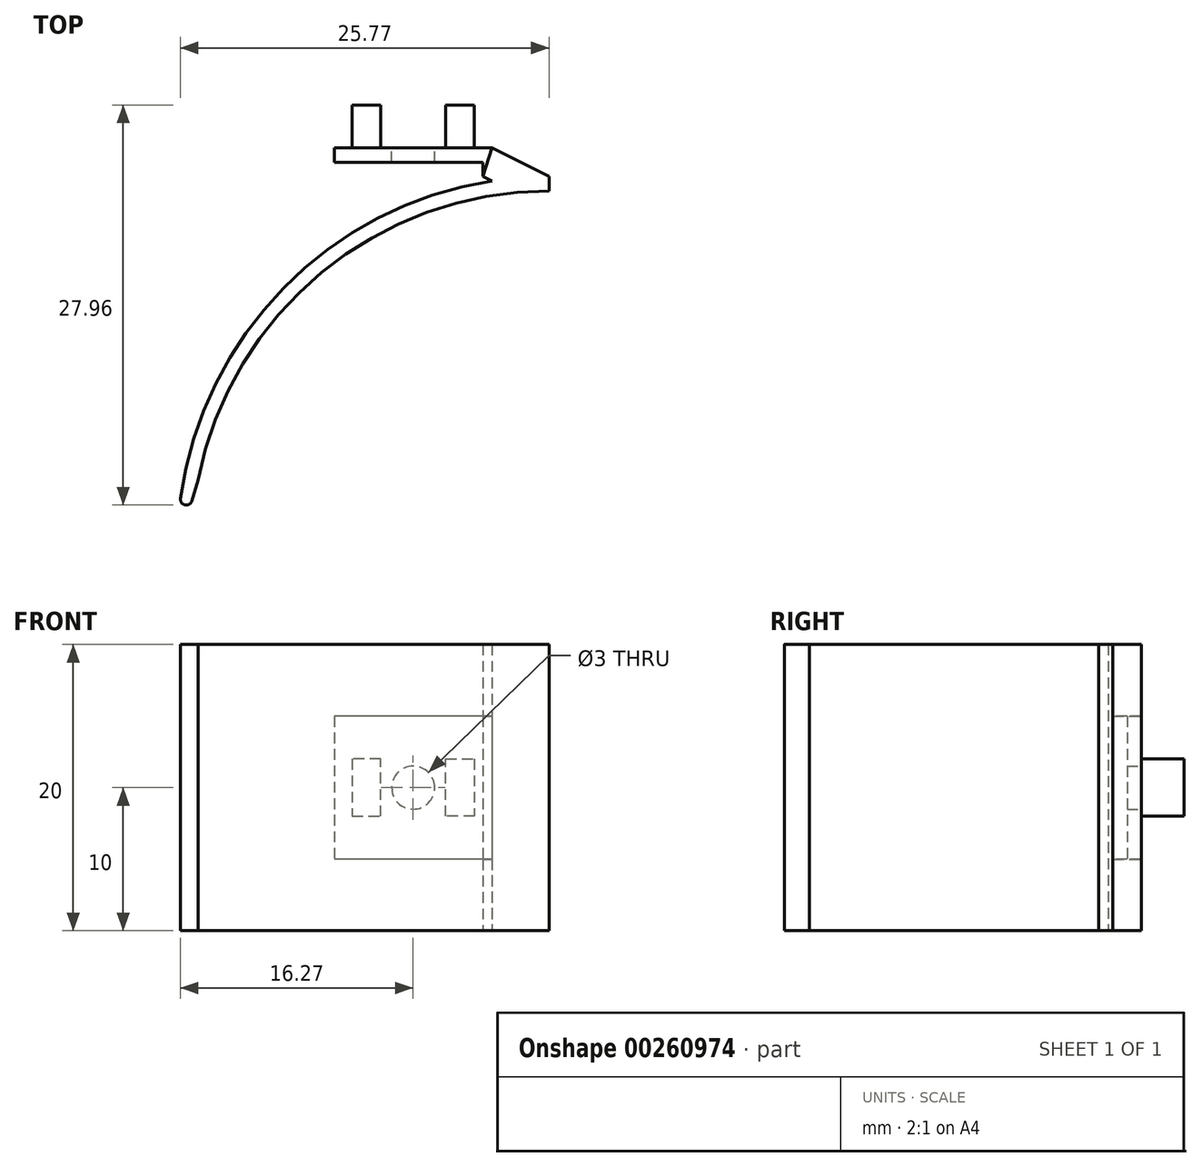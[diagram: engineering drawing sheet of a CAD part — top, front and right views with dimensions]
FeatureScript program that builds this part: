
annotation { "Feature Type Name" : "Feature", "Feature Type Description" : "" }
export const myFeature = defineFeature(function(context is Context, id is Id, definition is map)
    precondition{}
    {
        {
            var Q0;
            Q0=qCreatedBy(makeId("Top.planeOp"),FACE);
            var sketch = newSketch(context, id + "F0", { "sketchPlane" : qUnion([Q0])});
            skArc(sketch, "E0", {"start": v(0, 25) * mm, "mid": v(-15.9, 19.3) * mm, "end": v(-24.54, 4.8) * mm});
            skArc(sketch, "E1", {"start": v(-4, 25.7) * mm, "mid": v(-19.75, 16.91) * mm, "end": v(-26, 0) * mm});
            skLineSegment(sketch, "E2", {"start": v(0, 25) * mm, "end": v(0, 26) * mm});
            skLineSegment(sketch, "E3", {"start": v(-26, 0) * mm, "end": v(-24.54, 4.8) * mm});
            skLineSegment(sketch, "E4", {"start": v(-4, 28) * mm, "end": v(-15, 28) * mm});
            skLineSegment(sketch, "E5", {"start": v(-15, 28) * mm, "end": v(-15, 26) * mm});
            skLineSegment(sketch, "E6", {"start": v(-4.62, 26) * mm, "end": v(-15, 26) * mm});
            skPoint(sketch, "E7.orphan", {"position": v(-15, 25) * mm});
            skLineSegment(sketch, "E8", {"start": v(-4, 28) * mm, "end": v(0, 26) * mm});
            skLineSegment(sketch, "E9", {"start": v(-6, 28) * mm, "end": v(-8, 28) * mm});
            skLineSegment(sketch, "E10", {"start": v(-4, 25.7) * mm, "end": v(-4.62, 26) * mm});
            skSolve(sketch);
        }
        {
            var Q0;
            Q0=makeQuery(id+"F0.imprint","IMPRINT",FACE,{"disambiguationData":[TD([[makeQuery(id+"F0.imprint","IMPRINT",EDGE,{"derivedFrom":sQuery(id+"F0.wireOp",EDGE,"E0")}),-1.0]])]});
            extrude(context, id + "F1", {"entities" : qUnion([Q0]), "depth" : 20 * mm});
        }
        {
            var Q0;
            Q0=makeQuery(id+"F1.opExtrude","CAP_FACE",FACE,{"disambiguationData":[OSD([sQuery(id+"F0.wireOp",EDGE,"E0"),sQuery(id+"F0.wireOp",EDGE,"E1"),sQuery(id+"F0.wireOp",EDGE,"E2"),sQuery(id+"F0.wireOp",EDGE,"E3"),sQuery(id+"F0.wireOp",EDGE,"E4"),sQuery(id+"F0.wireOp",EDGE,"E5"),sQuery(id+"F0.wireOp",EDGE,"E6"),sQuery(id+"F0.wireOp",EDGE,"E8"),sQuery(id+"F0.wireOp",EDGE,"E9"),sQuery(id+"F0.wireOp",EDGE,"E10")])],"isStart":false});
            var sketch = newSketch(context, id + "F2", { "sketchPlane" : qUnion([Q0])});
            skLineSegment(sketch, "E11", {"start": v(-4.62, 26) * mm, "end": v(-4, 28) * mm});
            skSolve(sketch);
        }
        {
            var Q0;
            Q0=makeQuery(id+"F2.imprint","IMPRINT",FACE,{"disambiguationData":[TD([[makeQuery(id+"F2.imprint","IMPRINT",EDGE,{"derivedFrom":sQuery(id+"F2.wireOp",EDGE,"E11")}),1.0]])]});
            extrude(context, id + "F3", {"entities" : qUnion([Q0]), "operationType" : NewBodyOperationType.REMOVE, "oppositeDirection" : true, "depth" : 5 * mm});
        }
        {
            var Q0;
            Q0=makeQuery(id+"F1.opExtrude","CAP_FACE",FACE,{"disambiguationData":[OSD([sQuery(id+"F0.wireOp",EDGE,"E0"),sQuery(id+"F0.wireOp",EDGE,"E1"),sQuery(id+"F0.wireOp",EDGE,"E2"),sQuery(id+"F0.wireOp",EDGE,"E3"),sQuery(id+"F0.wireOp",EDGE,"E4"),sQuery(id+"F0.wireOp",EDGE,"E5"),sQuery(id+"F0.wireOp",EDGE,"E6"),sQuery(id+"F0.wireOp",EDGE,"E8"),sQuery(id+"F0.wireOp",EDGE,"E9"),sQuery(id+"F0.wireOp",EDGE,"E10")])],"isStart":true});
            var sketch = newSketch(context, id + "F4", { "sketchPlane" : qUnion([Q0])});
            skLineSegment(sketch, "E12", {"start": v(-4.62, -26) * mm, "end": v(-4, -28) * mm});
            skSolve(sketch);
        }
        {
            var Q0;
            Q0=makeQuery(id+"F4.imprint","IMPRINT",FACE,{"disambiguationData":[TD([[makeQuery(id+"F4.imprint","IMPRINT",EDGE,{"derivedFrom":sQuery(id+"F4.wireOp",EDGE,"E12")}),-1.0]])]});
            extrude(context, id + "F5", {"entities" : qUnion([Q0]), "operationType" : NewBodyOperationType.REMOVE, "oppositeDirection" : true, "depth" : 5 * mm});
        }
        {
            var Q0;
            Q0=makeQuery(id+"F1.opExtrude","SWEPT_FACE",FACE,{"disambiguationData":[OSD([sQuery(id+"F0.wireOp",EDGE,"E4"),sQuery(id+"F0.wireOp",EDGE,"E9")])]});
            var sketch = newSketch(context, id + "F6", { "sketchPlane" : qUnion([Q0])});
            skLineSegment(sketch, "E13", {"start": v(15, 10) * mm, "end": v(4, 10) * mm, "construction": true});
            skCircle(sketch, "E14", {"center": v(9.5, 10) * mm, "radius": 1.5 * mm});
            skSolve(sketch);
        }
        {
            var Q0;
            Q0=makeQuery(id+"F1.opExtrude","SWEPT_FACE",FACE,{"disambiguationData":[OSD([sQuery(id+"F0.wireOp",EDGE,"E4"),sQuery(id+"F0.wireOp",EDGE,"E9")])]});
            var sketch = newSketch(context, id + "F7", { "sketchPlane" : qUnion([Q0])});
            skLineSegment(sketch, "E15", {"start": v(4, 10) * mm, "end": v(15, 10) * mm, "construction": true});
            skCircle(sketch, "E16", {"center": v(9.5, 10) * mm, "radius": 1.55 * mm});
            skLineSegment(sketch, "E17", {"start": v(9.5, 10) * mm, "end": v(11.78, 10) * mm, "construction": true});
            skLineSegment(sketch, "E18", {"start": v(11.78, 10) * mm, "end": v(11.78, 12) * mm});
            skLineSegment(sketch, "E19", {"start": v(11.78, 12) * mm, "end": v(13.78, 12) * mm});
            skLineSegment(sketch, "E20", {"start": v(13.78, 12) * mm, "end": v(13.78, 8) * mm});
            skLineSegment(sketch, "E21", {"start": v(13.78, 8) * mm, "end": v(11.78, 8) * mm});
            skLineSegment(sketch, "E22", {"start": v(11.78, 8) * mm, "end": v(11.78, 10) * mm});
            skLineSegment(sketch, "E23", {"start": v(9.5, 10) * mm, "end": v(9.5, 13.7) * mm, "construction": true});
            skLineSegment(sketch, "E24.MirrorCS", {"start": v(7.22, 12) * mm, "end": v(5.22, 12) * mm});
            skLineSegment(sketch, "E25.MirrorCS", {"start": v(5.22, 12) * mm, "end": v(5.22, 8) * mm});
            skLineSegment(sketch, "E26.MirrorCS", {"start": v(5.22, 8) * mm, "end": v(7.22, 8) * mm});
            skLineSegment(sketch, "E27.MirrorCS", {"start": v(7.22, 10) * mm, "end": v(7.22, 12) * mm});
            skLineSegment(sketch, "E28.MirrorCS", {"start": v(7.22, 8) * mm, "end": v(7.22, 10) * mm});
            skSolve(sketch);
        }
        {
            var Q0;
            Q0=makeQuery(id+"F7.imprint","IMPRINT",FACE,{"disambiguationData":[TD([[makeQuery(id+"F7.imprint","IMPRINT",EDGE,{"derivedFrom":sQuery(id+"F7.wireOp",EDGE,"E18")}),-1.0]])]});
            var Q1;
            Q1=makeQuery(id+"F7.imprint","IMPRINT",FACE,{"disambiguationData":[TD([[makeQuery(id+"F7.imprint","IMPRINT",EDGE,{"derivedFrom":sQuery(id+"F7.wireOp",EDGE,"E24.MirrorCS")}),1.0]])]});
            extrude(context, id + "F8", {"entities" : qUnion([Q0, Q1]), "operationType" : NewBodyOperationType.ADD, "depth" : 3 * mm});
        }
        {
            var Q0;
            Q0=makeQuery(id+"F1.opExtrude","SWEPT_FACE",FACE,{"disambiguationData":[OSD([sQuery(id+"F0.wireOp",EDGE,"E6")])]});
            extrude(context, id + "F9", {"entities" : qUnion([Q0]), "operationType" : NewBodyOperationType.REMOVE, "oppositeDirection" : true, "depth" : 1 * mm});
        }
        {
            var Q0;
            Q0=makeQuery(id+"F6.imprint","IMPRINT",FACE,{"disambiguationData":[TD([[makeQuery(id+"F6.imprint","IMPRINT",EDGE,{"derivedFrom":sQuery(id+"F6.wireOp",EDGE,"E14")}),1.0]])]});
            var Q1;
            Q1=sQuery(id+"F6.wireOp",EDGE,"E14");
            extrude(context, id + "F10", {"entities" : qUnion([Q0]), "operationType" : NewBodyOperationType.REMOVE, "surfaceEntities" : qUnion([Q1]), "oppositeDirection" : true, "depth" : 1 * mm});
        }
        {
            var Q0;
            Q0=makeQuery(id+"F1.opExtrude","SWEPT_EDGE",EDGE,{"disambiguationData":[OSD([sQuery(id+"F0.wireOp",EDGE,"E1"),sQuery(id+"F0.wireOp",EDGE,"E3")])]});
            fillet(context, id + "F11", {"entities" : qUnion([Q0]), "radius" : 0.4 * mm, "tangentPropagation" : true, "allowEdgeOverflow" : false});
        }
    });
